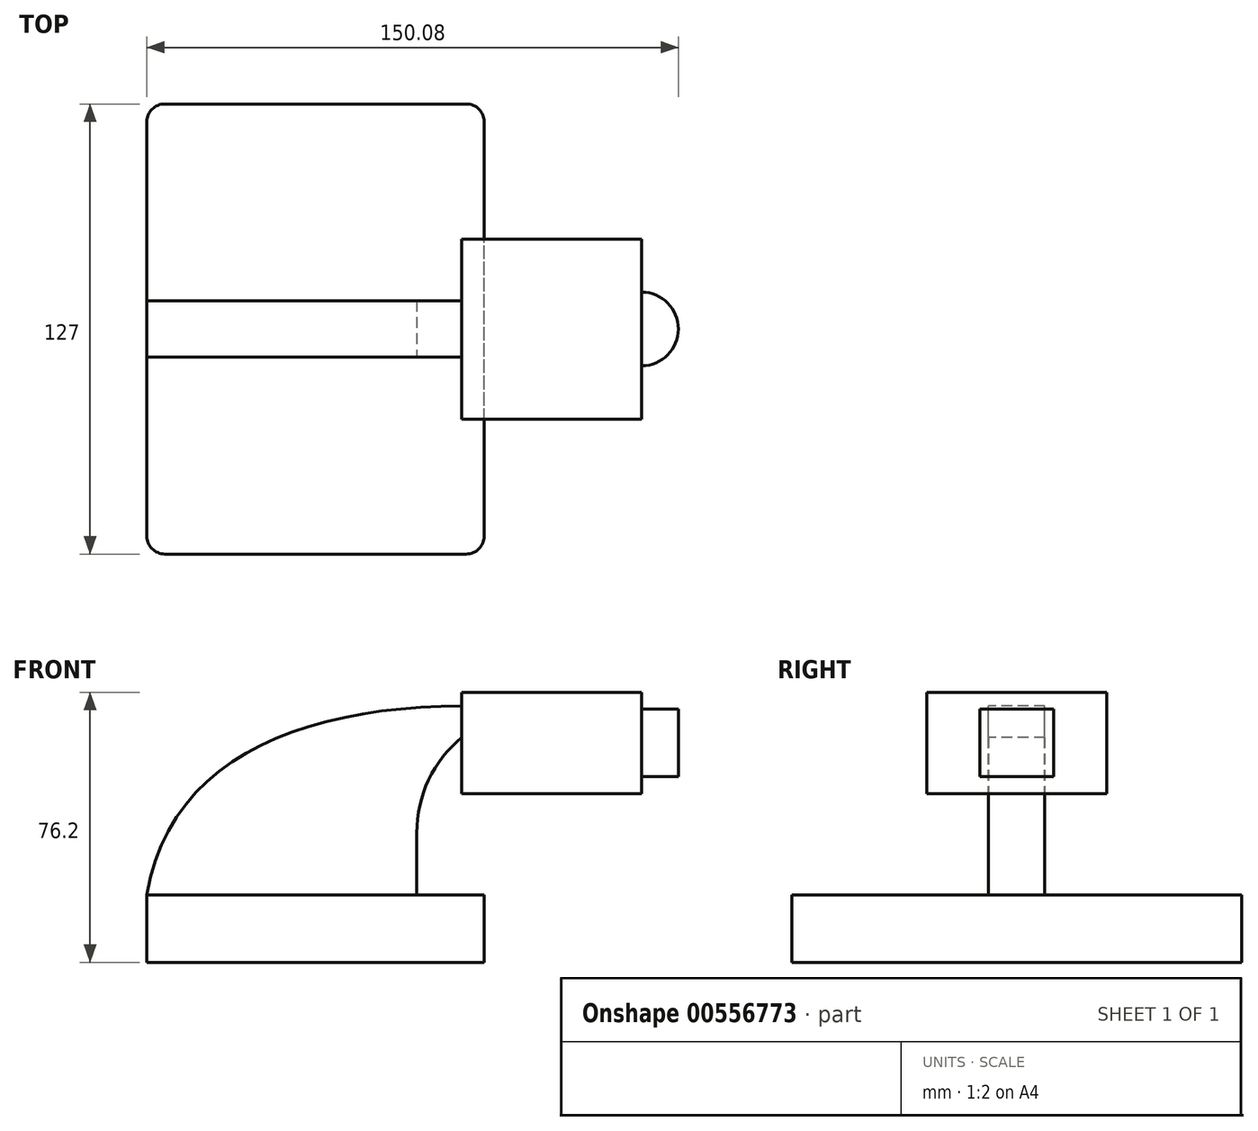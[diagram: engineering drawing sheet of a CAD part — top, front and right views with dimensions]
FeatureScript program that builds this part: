
annotation { "Feature Type Name" : "Feature", "Feature Type Description" : "" }
export const myFeature = defineFeature(function(context is Context, id is Id, definition is map)
    precondition{}
    {
        {
            var Q0;
            Q0=qCreatedBy(makeId("Front.planeOp"),FACE);
            var sketch = newSketch(context, id + "F0", { "sketchPlane" : qUnion([Q0])});
            skLineSegment(sketch, "E0.bottom", {"start": v(47.63, -9.53) * mm, "end": v(-47.62, -9.53) * mm});
            skLineSegment(sketch, "E0.top", {"start": v(47.62, 9.53) * mm, "end": v(-47.62, 9.52) * mm});
            skLineSegment(sketch, "E0.left", {"start": v(47.63, -9.53) * mm, "end": v(47.62, 9.53) * mm});
            skLineSegment(sketch, "E0.right", {"start": v(-47.62, -9.53) * mm, "end": v(-47.62, 9.52) * mm});
            skPoint(sketch, "E0.middle", {"position": v(0, 0) * mm});
            skLineSegment(sketch, "E1.bottom", {"start": v(92.08, 38.1) * mm, "end": v(41.28, 38.1) * mm});
            skLineSegment(sketch, "E1.top", {"start": v(92.08, 66.67) * mm, "end": v(41.28, 66.67) * mm});
            skLineSegment(sketch, "E1.left", {"start": v(92.08, 38.1) * mm, "end": v(92.08, 66.67) * mm});
            skLineSegment(sketch, "E1.right", {"start": v(41.28, 38.1) * mm, "end": v(41.28, 66.67) * mm});
            skPoint(sketch, "E1.middle", {"position": v(66.68, 52.39) * mm});
            skLineSegment(sketch, "E2", {"start": v(47.62, 9.53) * mm, "end": v(47.62, 27) * mm});
            skArc(sketch, "E3", {"start": v(47.63, 27) * mm, "mid": v(52.27, 38.23) * mm, "end": v(63.5, 42.88) * mm});
            skLineSegment(sketch, "E4", {"start": v(63.5, 42.88) * mm, "end": v(102.45, 42.88) * mm});
            skLineSegment(sketch, "E5.0", {"start": v(63.5, 61.93) * mm, "end": v(102.45, 61.93) * mm});
            skArc(sketch, "E5.1", {"start": v(28.58, 27) * mm, "mid": v(38.8, 51.7) * mm, "end": v(63.5, 61.93) * mm});
            skLineSegment(sketch, "E5.2", {"start": v(28.58, 9.53) * mm, "end": v(28.58, 27) * mm});
            skLineSegment(sketch, "E6", {"start": v(102.45, 42.88) * mm, "end": v(102.45, 61.93) * mm});
            skFitSpline(sketch, "E7", {"points": [v(-47.63, 9.52) * mm, v(63.5, 61.93) * mm], "startDerivative": vector(22.45, 134.96) * mm, "endDerivative": vector(162.47, -13.75) * mm});
            skSolve(sketch);
        }
        {
            var Q0;
            Q0=makeQuery(id+"F0.imprint","IMPRINT",FACE,{"disambiguationData":[TD([[makeQuery(id+"F0.imprint","IMPRINT",EDGE,{"derivedFrom":sQuery(id+"F0.wireOp",EDGE,"E0.bottom")}),-1.0]])]});
            extrude(context, id + "F1", {"entities" : qUnion([Q0]), "endBound" : BoundingType.SYMMETRIC, "depth" : 127 * mm, "offsetDistance" : 25.4 * mm});
        }
        {
            var Q0;
            {var subQ0=sQuery(id+"F0.wireOp",EDGE,"E5.2");Q0=makeQuery(id+"F0.imprint","IMPRINT",FACE,{"disambiguationData":[TD([[makeQuery(id+"F0.imprint","IMPRINT",EDGE,{"derivedFrom":subQ0}),1.0]])]});}
            extrude(context, id + "F2", {"entities" : qUnion([Q0]), "operationType" : NewBodyOperationType.ADD, "endBound" : BoundingType.SYMMETRIC, "oppositeDirection" : true, "depth" : 15.88 * mm, "offsetDistance" : 25.4 * mm});
        }
        {
            var Q0;
            {var subQ0=sQuery(id+"F0.wireOp",EDGE,"E1.left");var subQ1=sQuery(id+"F0.wireOp",EDGE,"E1.bottom");var subQ2=makeQuery(id+"F0.imprint","INTERSECT",VERTEX,{"derivedFrom":[subQ1,subQ0]});Q0=makeQuery(id+"F0.imprint","IMPRINT",FACE,{"disambiguationData":[TD([[makeQuery(id+"F0.imprint","IMPRINT",EDGE,{"disambiguationData":[TD([[subQ2,-1.0]])],"derivedFrom":subQ1}),-1.0]])]});}
            var Q1;
            {var subQ6=sQuery(id+"F0.wireOp",EDGE,"E1.top");Q1=makeQuery(id+"F0.imprint","IMPRINT",FACE,{"disambiguationData":[TD([[makeQuery(id+"F0.imprint","IMPRINT",EDGE,{"derivedFrom":subQ6}),1.0]])]});}
            var Q2;
            {var subQ0=sQuery(id+"F0.wireOp",EDGE,"E7");var subQ1=sQuery(id+"F0.wireOp",EDGE,"E1.right");var subQ2=makeQuery(id+"F0.imprint","INTERSECT",VERTEX,{"derivedFrom":[subQ1,subQ0]});Q2=makeQuery(id+"F0.imprint","IMPRINT",FACE,{"disambiguationData":[TD([[makeQuery(id+"F0.imprint","IMPRINT",EDGE,{"disambiguationData":[TD([[subQ2,1.0]])],"derivedFrom":subQ1}),-1.0]])]});}
            var Q3;
            {var subQ7=sQuery(id+"F0.wireOp",EDGE,"E1.bottom");var subQ9=sQuery(id+"F0.wireOp",EDGE,"E1.right");var subQ10=makeQuery(id+"F0.imprint","INTERSECT",VERTEX,{"derivedFrom":[subQ7,subQ9]});Q3=makeQuery(id+"F0.imprint","IMPRINT",FACE,{"disambiguationData":[TD([[makeQuery(id+"F0.imprint","IMPRINT",EDGE,{"disambiguationData":[TD([[subQ10,1.0]])],"derivedFrom":subQ7}),-1.0]])]});}
            extrude(context, id + "F3", {"entities" : qUnion([Q0, Q1, Q2, Q3]), "operationType" : NewBodyOperationType.ADD, "endBound" : BoundingType.SYMMETRIC, "depth" : 50.8 * mm, "offsetDistance" : 25.4 * mm});
        }
        {
            var Q0;
            {var subQ5=sQuery(id+"F0.wireOp",EDGE,"E6");Q0=makeQuery(id+"F0.imprint","IMPRINT",FACE,{"disambiguationData":[TD([[makeQuery(id+"F0.imprint","IMPRINT",EDGE,{"derivedFrom":subQ5}),1.0]])]});}
            var Q1;
            Q1=sQuery(id+"F0.wireOp",EDGE,"E1.left");
            revolve(context, id + "F4", {"operationType" : NewBodyOperationType.ADD, "entities" : qUnion([Q0]), "axis" : qUnion([Q1]), "revolveType" : RevolveType.FULL});
        }
        {
            var Q0;
            Q0=makeQuery(id+"F1.opExtrude","CAP_EDGE",EDGE,{"disambiguationData":[OSD([sQuery(id+"F0.wireOp",EDGE,"E0.right")])],"isStart":false});
            var Q1;
            Q1=makeQuery(id+"F1.opExtrude","CAP_EDGE",EDGE,{"disambiguationData":[OSD([sQuery(id+"F0.wireOp",EDGE,"E0.left")])],"isStart":false});
            var Q2;
            Q2=makeQuery(id+"F1.opExtrude","CAP_EDGE",EDGE,{"disambiguationData":[OSD([sQuery(id+"F0.wireOp",EDGE,"E0.left")])],"isStart":true});
            var Q3;
            Q3=makeQuery(id+"F1.opExtrude","CAP_EDGE",EDGE,{"disambiguationData":[OSD([sQuery(id+"F0.wireOp",EDGE,"E0.right")])],"isStart":true});
            fillet(context, id + "F5", {"entities" : qUnion([Q0, Q1, Q2, Q3]), "radius" : 5.08 * mm, "tangentPropagation" : true, "allowEdgeOverflow" : false});
        }
    });
